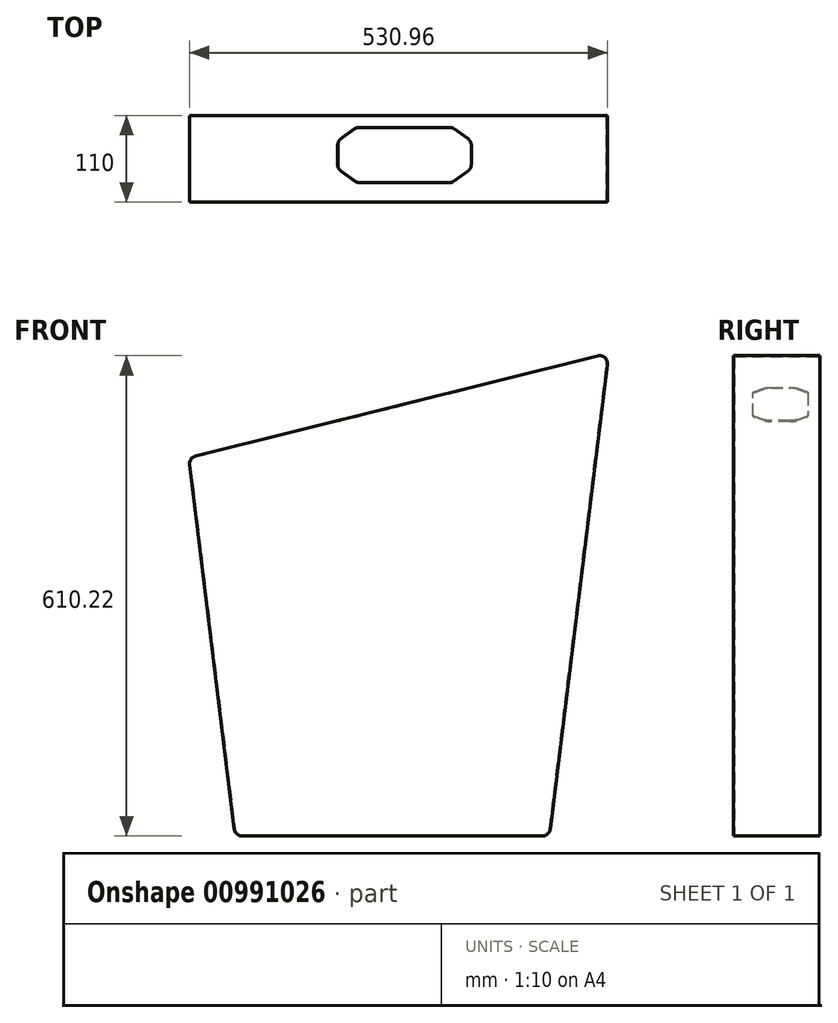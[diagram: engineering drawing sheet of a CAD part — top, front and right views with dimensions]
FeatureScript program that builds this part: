
annotation { "Feature Type Name" : "Feature", "Feature Type Description" : "" }
export const myFeature = defineFeature(function(context is Context, id is Id, definition is map)
    precondition{}
    {
        {
            var Q0;
            Q0=qCreatedBy(makeId("Front.planeOp"),FACE);
            var sketch = newSketch(context, id + "F0", { "sketchPlane" : qUnion([Q0])});
            skLineSegment(sketch, "E0", {"start": v(-171.4, -374.07) * mm, "end": v(210.26, -374.07) * mm});
            skLineSegment(sketch, "E1", {"start": v(220.19, -365.3) * mm, "end": v(292.66, 224.93) * mm});
            skLineSegment(sketch, "E2", {"start": v(280.31, 235.86) * mm, "end": v(-230.65, 108.46) * mm});
            skLineSegment(sketch, "E3", {"start": v(-238.15, 97.54) * mm, "end": v(-181.32, -365.3) * mm});
            skPoint(sketch, "E4.visualSharp", {"position": v(-239.23, 106.32) * mm});
            skArc(sketch, "E4.filletArc", {"start": v(-230.65, 108.46) * mm, "mid": v(-236.47, 104.42) * mm, "end": v(-238.15, 97.54) * mm});
            skPoint(sketch, "E5.visualSharp", {"position": v(294.43, 239.38) * mm});
            skArc(sketch, "E5.filletArc", {"start": v(292.66, 224.93) * mm, "mid": v(289.36, 233.64) * mm, "end": v(280.31, 235.86) * mm});
            skPoint(sketch, "E6.visualSharp", {"position": v(219.1, -374.07) * mm});
            skArc(sketch, "E6.filletArc", {"start": v(210.26, -374.07) * mm, "mid": v(216.89, -371.56) * mm, "end": v(220.19, -365.3) * mm});
            skPoint(sketch, "E7.visualSharp", {"position": v(-180.25, -374.07) * mm});
            skArc(sketch, "E7.filletArc", {"start": v(-181.32, -365.3) * mm, "mid": v(-178.03, -371.56) * mm, "end": v(-171.4, -374.07) * mm});
            skSolve(sketch);
        }
        {
            var Q0;
            Q0 = qSketchRegion(id + "F0", true);
            extrude(context, id + "F1", {"entities" : qUnion([Q0]), "endBound" : BoundingType.SYMMETRIC, "depth" : 110 * mm, "offsetDistance" : 25 * mm});
        }
        {
            var Q0;
            Q0=makeQuery(id+"F1.opExtrude","SWEPT_FACE",FACE,{"disambiguationData":[OSD([sQuery(id+"F0.wireOp",EDGE,"E0")])]});
            var Q1;
            Q1=makeQuery(id+"F1.opExtrude","SWEPT_BODY",BODY,{"disambiguationData":[OSD([sQuery(id+"F0.wireOp",EDGE,"E0"),sQuery(id+"F0.wireOp",EDGE,"E1"),sQuery(id+"F0.wireOp",EDGE,"E2"),sQuery(id+"F0.wireOp",EDGE,"E3")])]});
            shell(context, id + "F2", {"isHollow" : true, "entities" : qUnion([Q0]), "parts" : qUnion([Q1]), "thickness" : 1 * mm});
        }
        {
            var Q0;
            Q0=makeQuery(id+"F1.opExtrude","SWEPT_FACE",FACE,{"disambiguationData":[OSD([sQuery(id+"F0.wireOp",EDGE,"E2")])]});
            var sketch = newSketch(context, id + "F3", { "sketchPlane" : qUnion([Q0])});
            skLineSegment(sketch, "E8", {"start": v(-11.4, 17.22) * mm, "end": v(-11.4, -7.37) * mm});
            skLineSegment(sketch, "E9", {"start": v(-7.14, -15.56) * mm, "end": v(11.01, -28.27) * mm});
            skLineSegment(sketch, "E10", {"start": v(16.75, -30.08) * mm, "end": v(135.44, -30.08) * mm});
            skLineSegment(sketch, "E11", {"start": v(141.18, -28.27) * mm, "end": v(159.33, -15.56) * mm});
            skLineSegment(sketch, "E12", {"start": v(163.6, -7.37) * mm, "end": v(163.6, 17.22) * mm});
            skLineSegment(sketch, "E13", {"start": v(159.33, 25.4) * mm, "end": v(141.18, 38.12) * mm});
            skLineSegment(sketch, "E14", {"start": v(135.44, 39.92) * mm, "end": v(16.75, 39.92) * mm});
            skLineSegment(sketch, "E15", {"start": v(11.01, 38.12) * mm, "end": v(-7.14, 25.4) * mm});
            skPoint(sketch, "E16.visualSharp", {"position": v(-11.4, 22.42) * mm});
            skArc(sketch, "E16.filletArc", {"start": v(-7.14, 25.4) * mm, "mid": v(-10.27, 21.83) * mm, "end": v(-11.4, 17.22) * mm});
            skPoint(sketch, "E17.visualSharp", {"position": v(13.6, 39.92) * mm});
            skArc(sketch, "E17.filletArc", {"start": v(16.75, 39.92) * mm, "mid": v(13.74, 39.46) * mm, "end": v(11.01, 38.12) * mm});
            skPoint(sketch, "E18.visualSharp", {"position": v(-11.4, -12.58) * mm});
            skArc(sketch, "E18.filletArc", {"start": v(-11.4, -7.37) * mm, "mid": v(-10.27, -11.99) * mm, "end": v(-7.14, -15.56) * mm});
            skPoint(sketch, "E19.visualSharp", {"position": v(13.6, -30.08) * mm});
            skArc(sketch, "E19.filletArc", {"start": v(11.01, -28.27) * mm, "mid": v(13.74, -29.61) * mm, "end": v(16.75, -30.08) * mm});
            skPoint(sketch, "E20.visualSharp", {"position": v(138.6, 39.92) * mm});
            skArc(sketch, "E20.filletArc", {"start": v(141.18, 38.12) * mm, "mid": v(138.45, 39.46) * mm, "end": v(135.44, 39.92) * mm});
            skPoint(sketch, "E21.visualSharp", {"position": v(163.6, 22.42) * mm});
            skArc(sketch, "E21.filletArc", {"start": v(163.6, 17.22) * mm, "mid": v(162.47, 21.83) * mm, "end": v(159.33, 25.4) * mm});
            skPoint(sketch, "E22.visualSharp", {"position": v(163.6, -12.58) * mm});
            skArc(sketch, "E22.filletArc", {"start": v(159.33, -15.56) * mm, "mid": v(162.47, -11.99) * mm, "end": v(163.6, -7.37) * mm});
            skPoint(sketch, "E23.visualSharp", {"position": v(138.6, -30.08) * mm});
            skArc(sketch, "E23.filletArc", {"start": v(135.44, -30.08) * mm, "mid": v(138.45, -29.61) * mm, "end": v(141.18, -28.27) * mm});
            skSolve(sketch);
        }
        {
            var Q0;
            Q0 = qSketchRegion(id + "F3", true);
            extrude(context, id + "F4", {"entities" : qUnion([Q0]), "operationType" : NewBodyOperationType.REMOVE, "endBound" : BoundingType.UP_TO_NEXT, "oppositeDirection" : true, "depth" : 25 * mm, "offsetDistance" : 25 * mm});
        }
    });
